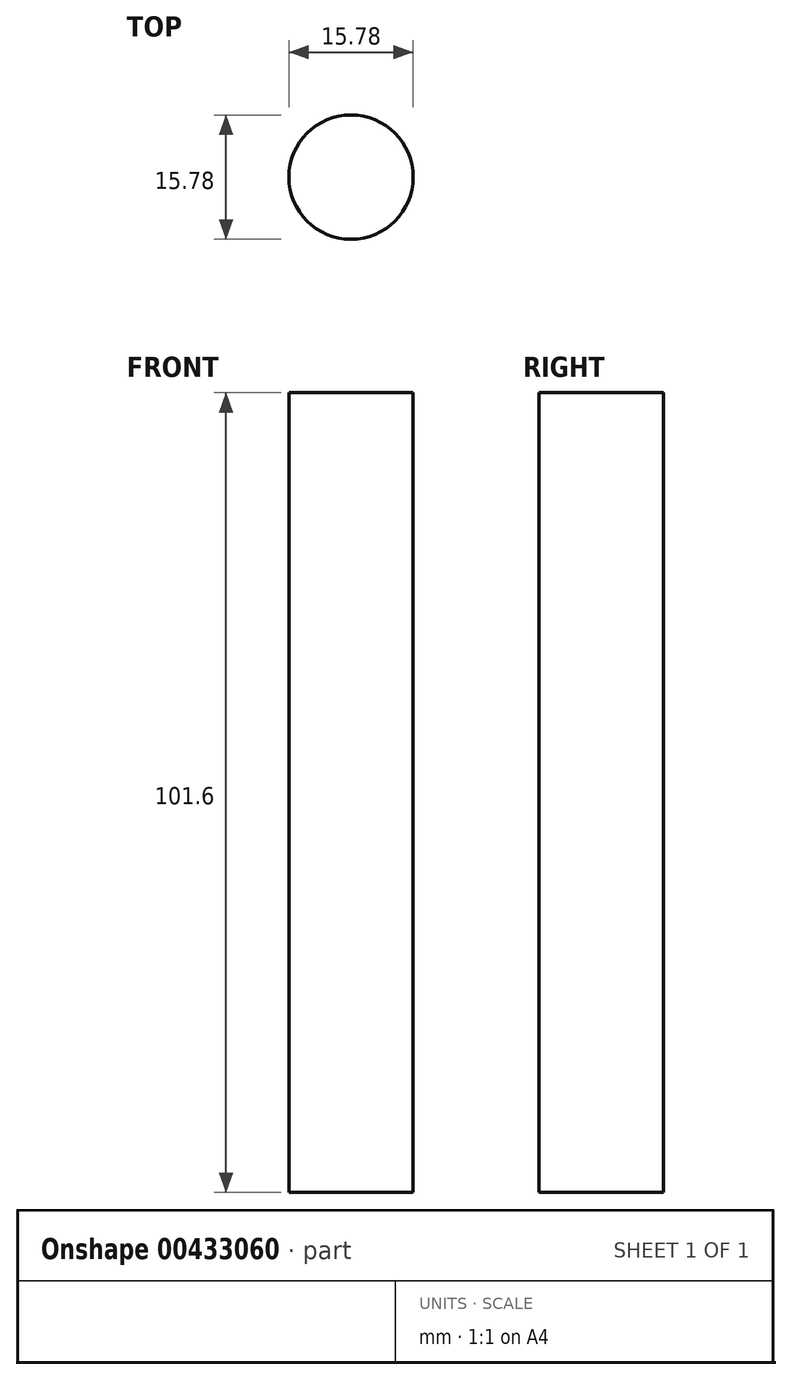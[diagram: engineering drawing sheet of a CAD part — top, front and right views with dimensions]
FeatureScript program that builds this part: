
annotation { "Feature Type Name" : "Feature", "Feature Type Description" : "" }
export const myFeature = defineFeature(function(context is Context, id is Id, definition is map)
    precondition{}
    {
        {
            var Q0;
            Q0=qCreatedBy(makeId("Top.planeOp"),FACE);
            var sketch = newSketch(context, id + "F0", { "sketchPlane" : qUnion([Q0])});
            skCircle(sketch, "E0", {"center": v(0, 0) * mm, "radius": 7.9 * mm});
            skSolve(sketch);
        }
        {
            var Q0;
            Q0=makeQuery(id+"F0.imprint","IMPRINT",FACE,{"disambiguationData":[TD([[makeQuery(id+"F0.imprint","IMPRINT",EDGE,{"derivedFrom":sQuery(id+"F0.wireOp",EDGE,"E0")}),1.0]])]});
            extrude(context, id + "F1", {"entities" : qUnion([Q0]), "depth" : 101.6 * mm});
        }
    });
